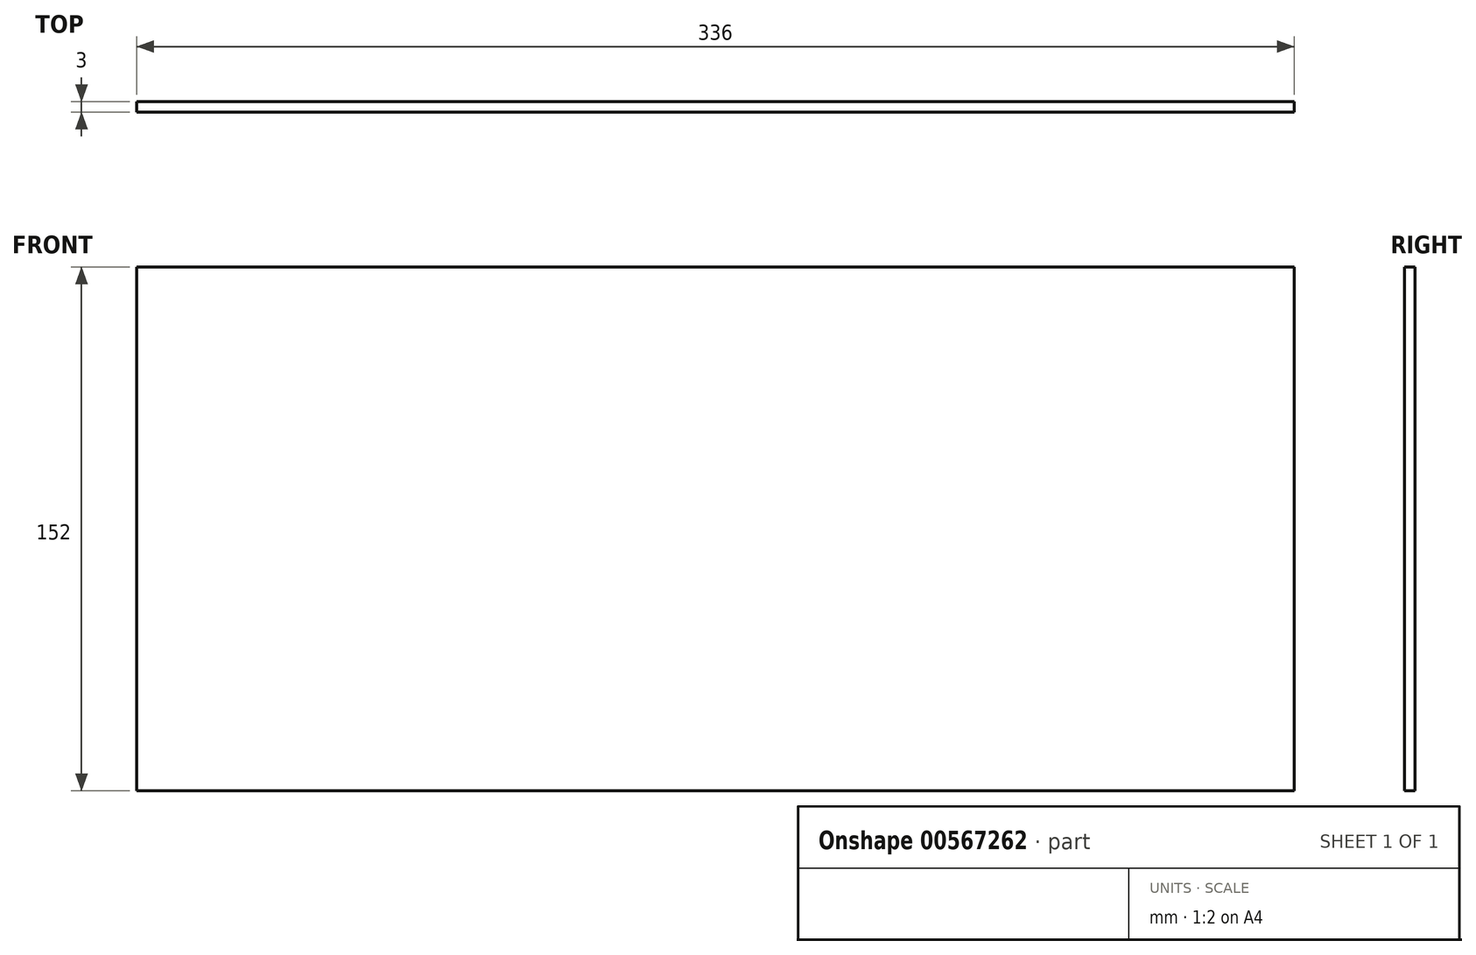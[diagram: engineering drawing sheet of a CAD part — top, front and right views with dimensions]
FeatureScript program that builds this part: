
annotation { "Feature Type Name" : "Feature", "Feature Type Description" : "" }
export const myFeature = defineFeature(function(context is Context, id is Id, definition is map)
    precondition{}
    {
        {
            var Q0;
            Q0=qCreatedBy(makeId("Front.planeOp"),FACE);
            var sketch = newSketch(context, id + "F0", { "sketchPlane" : qUnion([Q0])});
            skLineSegment(sketch, "E0.bottom", {"start": v(-179.61, 71.75) * mm, "end": v(156.39, 71.75) * mm});
            skLineSegment(sketch, "E0.top", {"start": v(-179.61, -80.25) * mm, "end": v(156.39, -80.25) * mm});
            skLineSegment(sketch, "E0.left", {"start": v(-179.61, 71.75) * mm, "end": v(-179.61, -80.25) * mm});
            skLineSegment(sketch, "E0.right", {"start": v(156.39, 71.75) * mm, "end": v(156.39, -80.25) * mm});
            skSolve(sketch);
        }
        {
            var Q0;
            Q0=makeQuery(id+"F0.imprint","IMPRINT",FACE,{"disambiguationData":[TD([[makeQuery(id+"F0.imprint","IMPRINT",EDGE,{"derivedFrom":sQuery(id+"F0.wireOp",EDGE,"E0.bottom")}),-1.0]])]});
            extrude(context, id + "F1", {"entities" : qUnion([Q0]), "depth" : 3 * mm, "offsetDistance" : 25 * mm});
        }
    });
